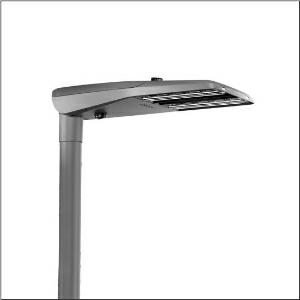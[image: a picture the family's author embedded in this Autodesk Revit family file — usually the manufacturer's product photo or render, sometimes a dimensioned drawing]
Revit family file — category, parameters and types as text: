
# Revit family: streetlight_sl_11_iq_midi___st1_2a_5xc3a41y08me_bddd
name_source: partatom
category: Lighting Fixtures
units: mm (PartAtom-declared; Revit-internal decimal feet)

## family parameters
Cut with Voids When Loaded = No
Host = Face
Light Source = No
Part Type = Normal
Room Calculation Point = No
Round Connector Dimension = Use Diameter
Shared = No

## types (1)
- --- (1 x LED, 18900 lm, 122.6 W, 4000K)
    Apparent Load = 123 VA
    CIE Flux Codes = 32 70 96 100 100
    Color Rendering = 70
    Color Temperature = 4000K
    Default Elevation = 1800 mm
    Description = Streetlight SL 11 iQ midi, mast luminaire, primary light control with 3 zone facetted reflector, of plastic, silver coated, highly specular, primary optical cover: cover, of PMMA, transparent, light distribution: ST1.2a, light emission: direct distribution, primary light characteristic: asymmetric, installation type: post-top, side-entry, lamps: LED, High Power LED, rated values: 18.900lm | 122,6W | 154,2lm/W (begin service life); end service life: 18.900lm | 130,2W; at 50% lumin. flux: 9.450lm | 56,3W | 167,9lm/W, colour temperature: 4000K, colour rendering: CRI > 70, light colour: 740, light setting 1 begin service life: 100% | 18.900lm | 122,6W | 154,2lm/W | 4.000K, light setting 1 end service life: 130,2W, further light settings possible, control: pre-setting: logarithmic dimming characteristic, Street-Remote, Auto-Match, Temp-Guard, Lumen-Switch, Night-Set, Smart-Wire, Light-Fading, Desk-Remote (wireless, voltage-free reading and setting of iQ features in the workshop via application-optimized NFC function/RFID function), optimised constant luminous flux control (CLO 2.0), with cable H07RN-F 5x 1.5mm², mains connection: 230..240V, AC, 50/60Hz, connection cable pre-assembled, cable length: 12,5m, luminaire housing, of diecast aluminium, powder-coated, Siteco® metallic grey (DB 702S), please order mast flange separately, inclination adjustable without tools: 0°, 5°, 10°, 15° (post-top) | 0°, -5°, -10°, -15° (side-entry), sealing non-destructively replaceable, multi-level sealing system, length: 780mm, width: 376mm, height: 118mm, mast flange for spigot size: 42mm (side-entry): 5XC10008XM4, 60/48mm (side-entry/post-top): 5XC10108XM2, 76/60mm (side-entry/post-top): 5XC10108XM1, equipment: Power, Smart Interface below and above, protection rating (complete): IP66, insulation class (complete): insulation class II (safety insulation), certification: CE, ENEC, ENEC+, VDE, UKCA, impact resistance: IK10, permissible operating ambient temperature for outdoor applications: -25..+50°C, standard-compliant lighting for roads and squares, Environmental Product Declaration (EPD) tested and certified by an independent institute, packaging unit: 1 piece

Light Distribution: ST1.2a
    Height = 118 mm
    Lamp = 1 x LED
    Lamp Light Flux = 18900 lm
    Lamp Power = 122.6 W
    Lamp count = 1
    Length = 780 mm
    Luminous efficacy = 154 lm/W
    Manufacturer = Siteco
    ModVariant = No
    Model = 5XC3A41Y08ME
    Number of Poles = 1
    OnlyDefault = Yes
    Power Factor = 1
    Product Name = Streetlight SL 11 iQ midi | ST1.2a
    Product group = mast luminaire | pylon top
    ProductGroupID = 6100
    Protection Class = Protection class II
    Protection Degree = IP 66
    RLX_Detail_Level = 1
    RLX_Emergency_Light_Flux = 0 lm
    RLX_Emergency_Type = 0
    RLX_Emergency_Type_DB = No
    RlxData = <blob elided: 69969 chars, md5=ceeb1579>
    Socket = socket
    Standby Power = 0 W
    System Light Flux = 18900 lm
    System Power = 123 W
    Type Comments = factory setting: luminous flux: 100 % | dim-lin: 254 | 552 mA
    Type Image = l_1004429.jpg
    URL = http://relux.com
    VarID = @adj_154631
    Voltage = 0 V
    Weight = 0.00 kg
    Width = 376 mm

## geometry (parser evidence)
native form markers: Blend x4, Sweep x9
no freeform markers — native parametric forms only
